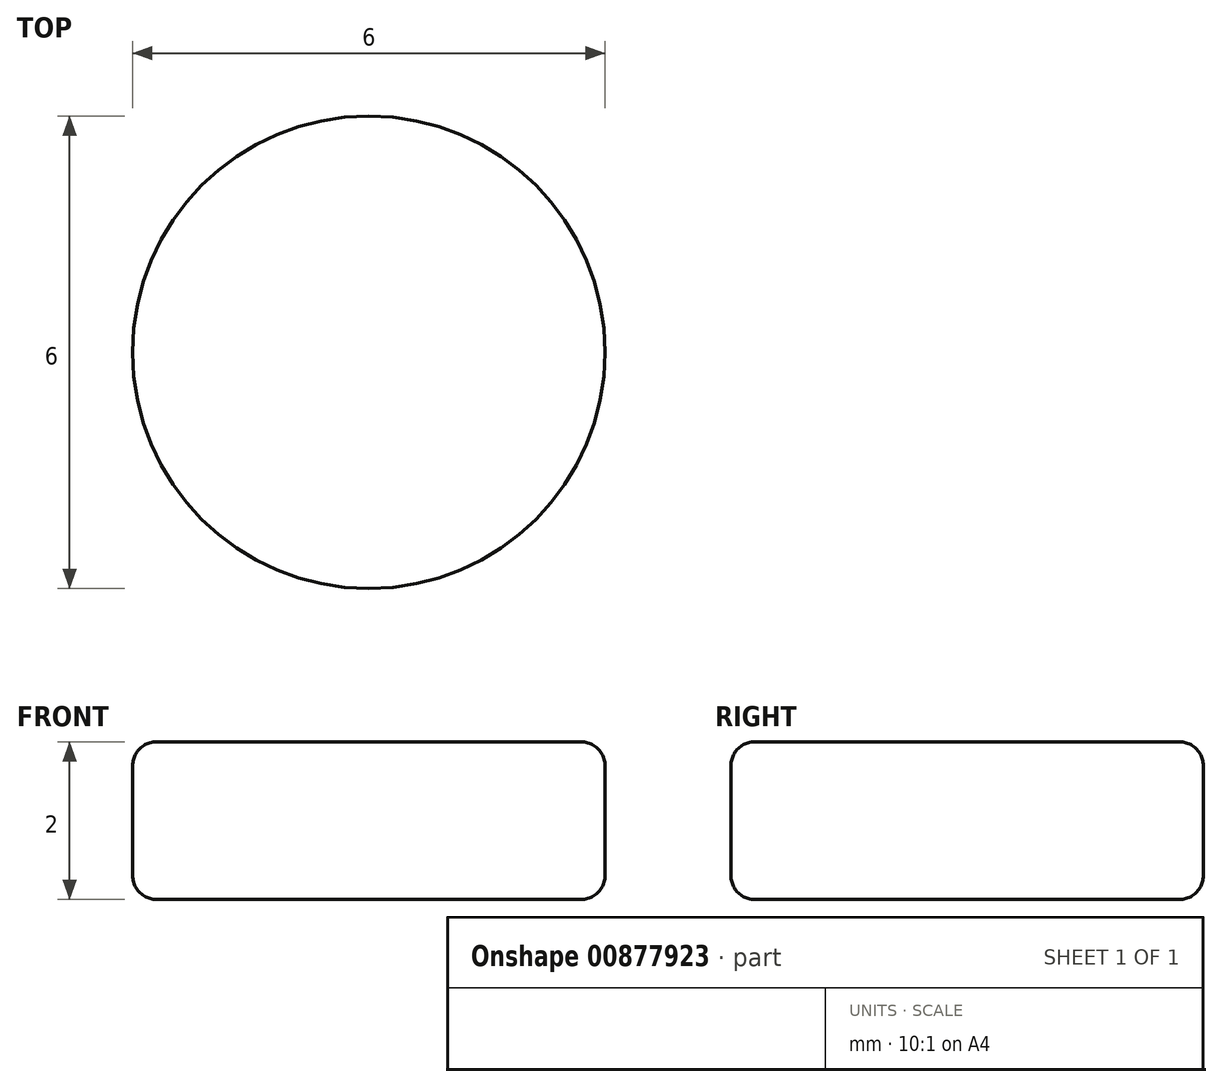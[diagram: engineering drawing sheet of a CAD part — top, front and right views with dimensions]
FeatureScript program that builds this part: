
annotation { "Feature Type Name" : "Feature", "Feature Type Description" : "" }
export const myFeature = defineFeature(function(context is Context, id is Id, definition is map)
    precondition{}
    {
        {
            var Q0;
            Q0=qCreatedBy(makeId("Top.planeOp"),FACE);
            var sketch = newSketch(context, id + "F0", { "sketchPlane" : qUnion([Q0])});
            skCircle(sketch, "E0", {"center": v(0, 0) * mm, "radius": 3 * mm});
            skSolve(sketch);
        }
        {
            var Q0;
            Q0 = qSketchRegion(id + "F0", true);
            extrude(context, id + "F1", {"entities" : qUnion([Q0]), "depth" : 2 * mm, "offsetDistance" : 25 * mm});
        }
        {
            var Q0;
            Q0=makeQuery(id+"F1.opExtrude","CAP_EDGE",EDGE,{"disambiguationData":[OSD([sQuery(id+"F0.wireOp",EDGE,"E0")])],"isStart":true});
            var Q1;
            Q1=makeQuery(id+"F1.opExtrude","CAP_EDGE",EDGE,{"disambiguationData":[OSD([sQuery(id+"F0.wireOp",EDGE,"E0")])],"isStart":false});
            fillet(context, id + "F2", {"entities" : qUnion([Q0, Q1]), "radius" : .3 * mm, "tangentPropagation" : true, "allowEdgeOverflow" : false});
        }
    });
